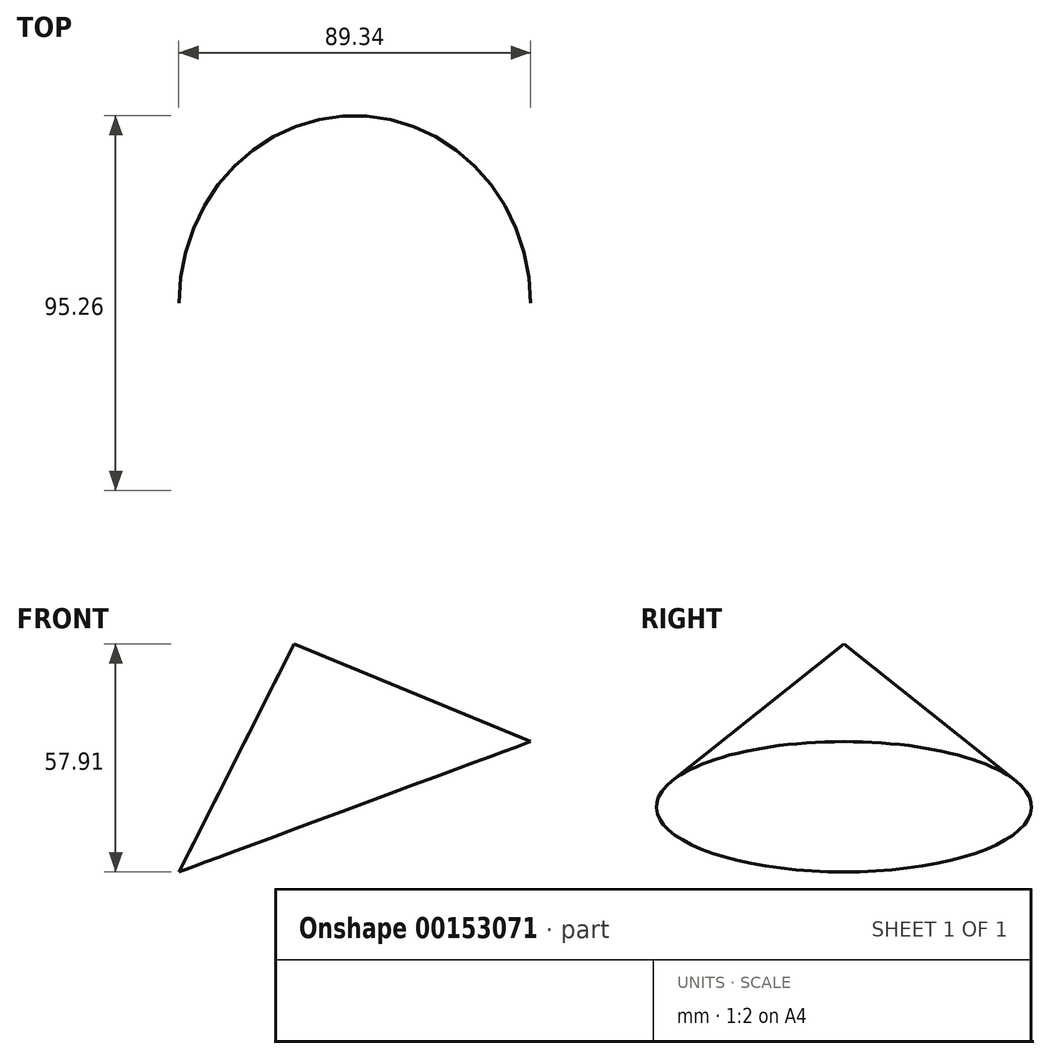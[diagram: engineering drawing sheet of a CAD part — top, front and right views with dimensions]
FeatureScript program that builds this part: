
annotation { "Feature Type Name" : "Feature", "Feature Type Description" : "" }
export const myFeature = defineFeature(function(context is Context, id is Id, definition is map)
    precondition{}
    {
        {
            var Q0;
            Q0=qCreatedBy(makeId("Front.planeOp"),FACE);
            var sketch = newSketch(context, id + "F0", { "sketchPlane" : qUnion([Q0])});
            skLineSegment(sketch, "E0", {"start": v(-25.72, -16.38) * mm, "end": v(25.08, -16.38) * mm});
            skLineSegment(sketch, "E1", {"start": v(25.08, -16.38) * mm, "end": v(3.62, 41.53) * mm});
            skLineSegment(sketch, "E2", {"start": v(3.62, 41.53) * mm, "end": v(-25.72, -16.38) * mm});
            skSolve(sketch);
        }
        {
            var Q0;
            Q0=sQuery(id+"F0.wireOp",EDGE,"E2");
            var Q1;
            Q1=sQuery(id+"F0.wireOp",EDGE,"E1");
            revolve(context, id + "F1", {"bodyType" : ToolBodyType.SURFACE, "surfaceEntities" : qUnion([Q0]), "axis" : qUnion([Q1]), "revolveType" : RevolveType.FULL});
        }
    });
